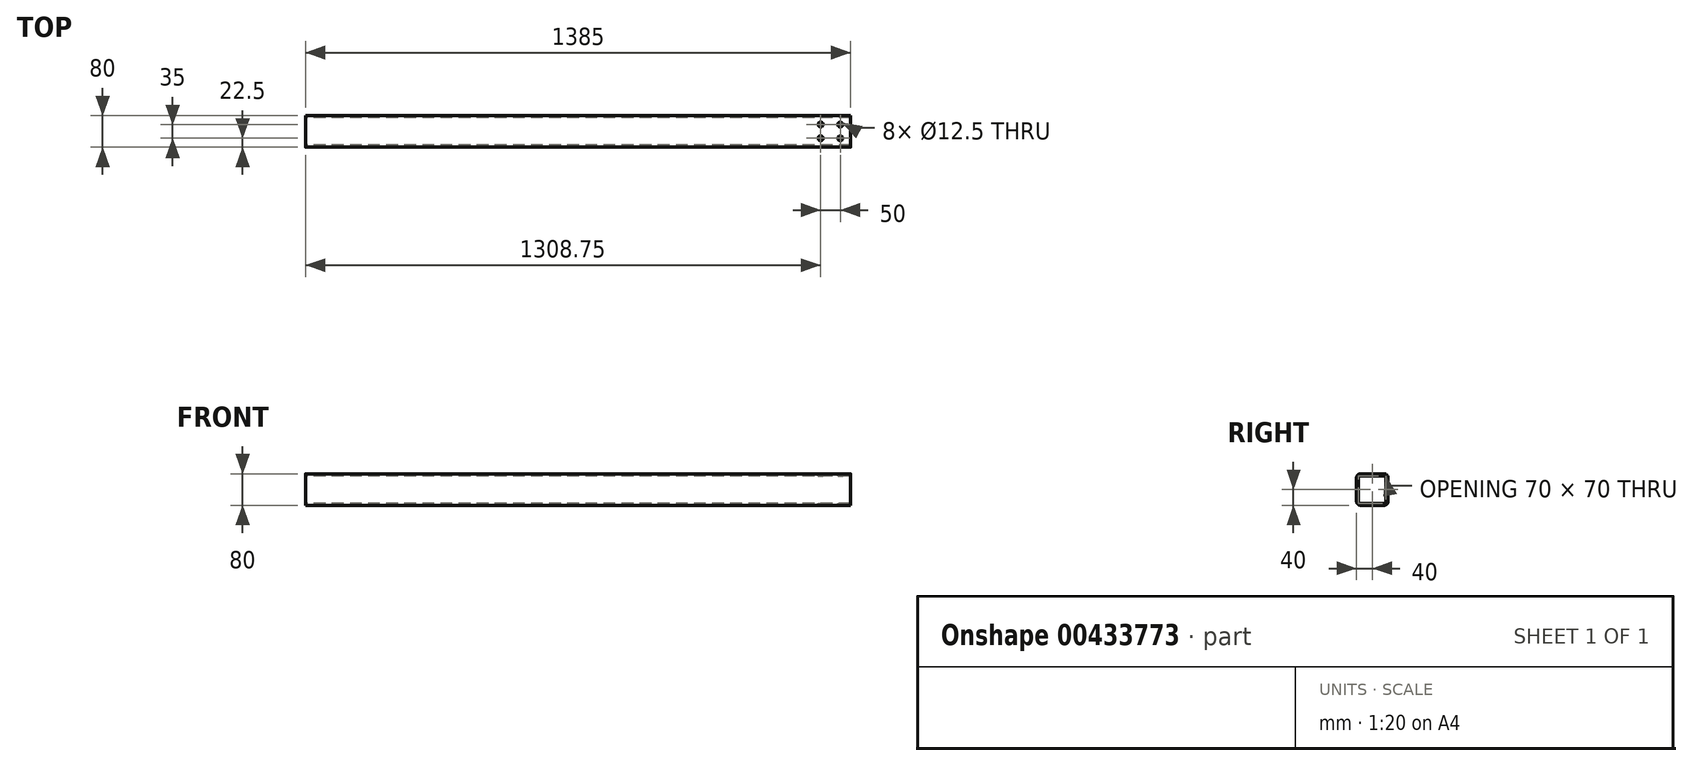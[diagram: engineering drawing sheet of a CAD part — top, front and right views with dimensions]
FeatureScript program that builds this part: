
annotation { "Feature Type Name" : "Feature", "Feature Type Description" : "" }
export const myFeature = defineFeature(function(context is Context, id is Id, definition is map)
    precondition{}
    {
        {
            var Q0;
            Q0=qCreatedBy(makeId("Right.planeOp"),FACE);
            var sketch = newSketch(context, id + "F0", { "sketchPlane" : qUnion([Q0])});
            skLineSegment(sketch, "E0.bottom", {"start": v(30, 40) * mm, "end": v(-30, 40) * mm});
            skLineSegment(sketch, "E0.top", {"start": v(30, -40) * mm, "end": v(-30, -40) * mm});
            skLineSegment(sketch, "E0.left", {"start": v(40, 30) * mm, "end": v(40, -30) * mm});
            skLineSegment(sketch, "E0.right", {"start": v(-40, 30) * mm, "end": v(-40, -30) * mm});
            skPoint(sketch, "E0.middle", {"position": v(0, 0) * mm});
            skPoint(sketch, "E1.visualSharp", {"position": v(-40, 40) * mm});
            skArc(sketch, "E1.filletArc", {"start": v(-30, 40) * mm, "mid": v(-37.07, 37.07) * mm, "end": v(-40, 30) * mm});
            skPoint(sketch, "E2.visualSharp", {"position": v(40, 40) * mm});
            skArc(sketch, "E2.filletArc", {"start": v(40, 30) * mm, "mid": v(37.07, 37.07) * mm, "end": v(30, 40) * mm});
            skPoint(sketch, "E3.visualSharp", {"position": v(40, -40) * mm});
            skArc(sketch, "E3.filletArc", {"start": v(30, -40) * mm, "mid": v(37.07, -37.07) * mm, "end": v(40, -30) * mm});
            skPoint(sketch, "E4.visualSharp", {"position": v(-40, -40) * mm});
            skArc(sketch, "E4.filletArc", {"start": v(-40, -30) * mm, "mid": v(-37.07, -37.07) * mm, "end": v(-30, -40) * mm});
            skArc(sketch, "E5.0", {"start": v(35, 30) * mm, "mid": v(33.54, 33.54) * mm, "end": v(30, 35) * mm});
            skLineSegment(sketch, "E5.1", {"start": v(35, 30) * mm, "end": v(35, -30) * mm});
            skLineSegment(sketch, "E5.2", {"start": v(30, 35) * mm, "end": v(-30, 35) * mm});
            skArc(sketch, "E5.3", {"start": v(30, -35) * mm, "mid": v(33.54, -33.54) * mm, "end": v(35, -30) * mm});
            skArc(sketch, "E5.4", {"start": v(-30, 35) * mm, "mid": v(-33.54, 33.54) * mm, "end": v(-35, 30) * mm});
            skLineSegment(sketch, "E5.5", {"start": v(-35, 30) * mm, "end": v(-35, -30) * mm});
            skArc(sketch, "E5.6", {"start": v(-35, -30) * mm, "mid": v(-33.54, -33.54) * mm, "end": v(-30, -35) * mm});
            skLineSegment(sketch, "E5.7", {"start": v(30, -35) * mm, "end": v(-30, -35) * mm});
            skSolve(sketch);
        }
        {
            var Q0;
            Q0 = qSketchRegion(id + "F0", true);
            extrude(context, id + "F1", {"entities" : qUnion([Q0]), "depth" : 1385 * mm});
        }
        {
            var Q0;
            Q0=qCreatedBy(makeId("Top.planeOp"),FACE);
            var sketch = newSketch(context, id + "F2", { "sketchPlane" : qUnion([Q0])});
            skCircle(sketch, "E6", {"center": v(1358.75, -17.5) * mm, "radius": 6.25 * mm});
            skLineSegment(sketch, "E7", {"start": v(1380.2, 0) * mm, "end": v(1158.8, 0) * mm, "construction": true});
            skCircle(sketch, "E8.1.0.0", {"center": v(1308.75, -17.5) * mm, "radius": 6.25 * mm});
            skLineSegment(sketch, "E8.direction1", {"start": v(1358.75, -17.5) * mm, "end": v(1308.75, -17.5) * mm, "construction": true});
            skCircle(sketch, "E9.MirrorC", {"center": v(1358.75, 17.5) * mm, "radius": 6.25 * mm});
            skCircle(sketch, "E10.MirrorC", {"center": v(1308.75, 17.5) * mm, "radius": 6.25 * mm});
            skSolve(sketch);
        }
        {
            var Q0;
            Q0 = qSketchRegion(id + "F2", true);
            extrude(context, id + "F3", {"entities" : qUnion([Q0]), "operationType" : NewBodyOperationType.REMOVE, "endBound" : BoundingType.THROUGH_ALL, "oppositeDirection" : true, "depth" : 25 * mm, "hasSecondDirection" : true, "secondDirectionBound" : SecondDirectionBoundingType.THROUGH_ALL, "secondDirectionOppositeDirection" : false, "secondDirectionDepth" : 25 * mm});
        }
    });
